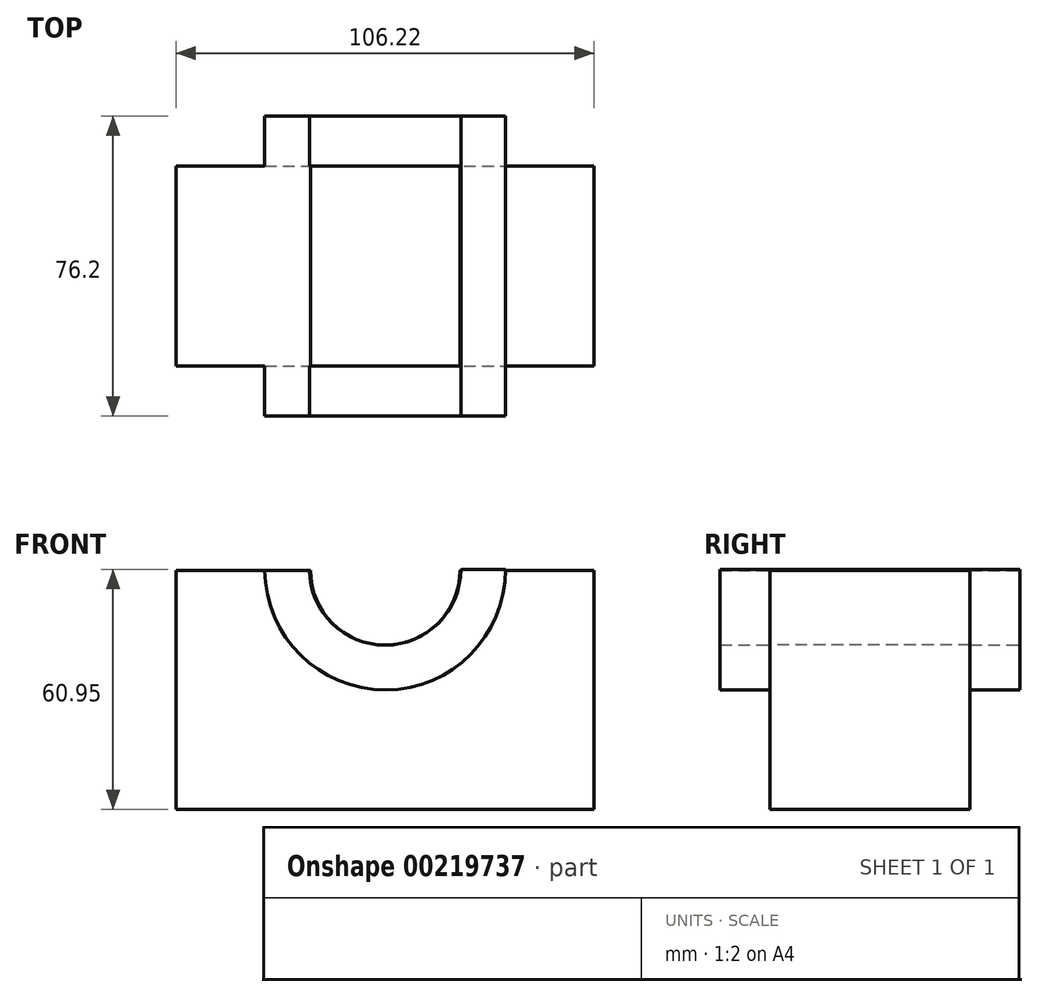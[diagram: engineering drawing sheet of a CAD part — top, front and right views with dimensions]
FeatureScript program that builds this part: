
annotation { "Feature Type Name" : "Feature", "Feature Type Description" : "" }
export const myFeature = defineFeature(function(context is Context, id is Id, definition is map)
    precondition{}
    {
        {
            var Q0;
            Q0=qCreatedBy(makeId("Front.planeOp"),FACE);
            var sketch = newSketch(context, id + "F0", { "sketchPlane" : qUnion([Q0])});
            skLineSegment(sketch, "E0.bottom", {"start": v(53.1, -30.36) * mm, "end": v(-53.1, -30.36) * mm});
            skLineSegment(sketch, "E0.left", {"start": v(53.1, -30.36) * mm, "end": v(53.1, 30.36) * mm});
            skLineSegment(sketch, "E0.right", {"start": v(-53.1, -30.36) * mm, "end": v(-53.1, 30.36) * mm});
            skPoint(sketch, "E0.middle", {"position": v(0, 0) * mm});
            skLineSegment(sketch, "E1", {"start": v(-53.1, 30.36) * mm, "end": v(53.1, 30.36) * mm});
            skSolve(sketch);
        }
        {
            var Q0;
            Q0=makeQuery(id+"F0.imprint","IMPRINT",FACE,{"disambiguationData":[TD([[makeQuery(id+"F0.imprint","IMPRINT",EDGE,{"derivedFrom":sQuery(id+"F0.wireOp",EDGE,"E0.bottom")}),-1.0]])]});
            extrude(context, id + "F1", {"entities" : qUnion([Q0]), "endBound" : BoundingType.SYMMETRIC, "depth" : 50.8 * mm});
        }
        {
            var Q0;
            Q0=qCreatedBy(makeId("Front.planeOp"),FACE);
            var sketch = newSketch(context, id + "F2", { "sketchPlane" : qUnion([Q0])});
            skArc(sketch, "E2", {"start": v(-30.6, 30.37) * mm, "mid": v(0.11, 0) * mm, "end": v(30.6, 30.6) * mm});
            skArc(sketch, "E3", {"start": v(-19.21, 30.37) * mm, "mid": v(0.11, 11.38) * mm, "end": v(19.21, 30.6) * mm});
            skLineSegment(sketch, "E4", {"start": v(-19.21, 30.37) * mm, "end": v(-30.6, 30.37) * mm});
            skLineSegment(sketch, "E5", {"start": v(19.21, 30.6) * mm, "end": v(30.6, 30.6) * mm});
            skSolve(sketch);
        }
        {
            var Q0;
            Q0 = qSketchRegion(id + "F2", true);
            extrude(context, id + "F3", {"entities" : qUnion([Q0]), "operationType" : NewBodyOperationType.ADD, "endBound" : BoundingType.SYMMETRIC, "depth" : 76.2 * mm});
        }
        {
            var Q0;
            {var subQ0=sQuery(id+"F0.wireOp",EDGE,"E1");Q0=makeQuery(id+"F3.boolean.opBoolean","SPLIT",FACE,{"disambiguationData":[TD([makeQuery(id+"F3.opExtrude","SWEPT_FACE",FACE,{"disambiguationData":[OSD([sQuery(id+"F2.wireOp",EDGE,"E3")])]})])],"derivedFrom":makeQuery(id+"F1.opExtrude","CAP_FACE",FACE,{"disambiguationData":[OSD([sQuery(id+"F0.wireOp",EDGE,"E0.bottom"),sQuery(id+"F0.wireOp",EDGE,"E0.left"),sQuery(id+"F0.wireOp",EDGE,"E0.right"),subQ0])],"isStart":false})});}
            var sketch = newSketch(context, id + "F4", { "sketchPlane" : qUnion([Q0])});
            skCircle(sketch, "E6", {"center": v(0, 30.36) * mm, "radius": 18.98 * mm});
            skSolve(sketch);
        }
        {
            var Q0;
            {var subQ0=sQuery(id+"F4.wireOp",EDGE,"E6");var subQ1=sQuery(id+"F0.wireOp",EDGE,"E1");var subQ2=makeQuery(id+"F1.opExtrude","CAP_FACE",FACE,{"disambiguationData":[OSD([sQuery(id+"F0.wireOp",EDGE,"E0.bottom"),sQuery(id+"F0.wireOp",EDGE,"E0.left"),sQuery(id+"F0.wireOp",EDGE,"E0.right"),subQ1])],"isStart":false});var subQ3=makeQuery(id+"F3.opExtrude","SWEPT_FACE",FACE,{"disambiguationData":[OSD([sQuery(id+"F2.wireOp",EDGE,"E3")])]});var subQ6=makeQuery(id+"F4.imprint","INTERSECT",VERTEX,{"derivedFrom":[makeQuery(id+"F3.boolean.opBoolean","INTERSECT",EDGE,{"derivedFrom":[subQ2,subQ3]}),subQ0]});Q0=makeQuery(id+"F4.imprint","IMPRINT",FACE,{"disambiguationData":[TD([[makeQuery(id+"F4.imprint","IMPRINT",EDGE,{"disambiguationData":[TD([[subQ6,1.0]])],"derivedFrom":subQ0}),1.0]])]});}
            var Q1;
            {var subQ0=sQuery(id+"F4.wireOp",EDGE,"E6");var subQ1=sQuery(id+"F0.wireOp",EDGE,"E1");var subQ2=makeQuery(id+"F3.boolean.opBoolean","SPLIT",EDGE,{"disambiguationData":[TD([makeQuery(id+"F3.opExtrude","SWEPT_FACE",FACE,{"disambiguationData":[OSD([sQuery(id+"F2.wireOp",EDGE,"E3")])]})])],"derivedFrom":makeQuery(id+"F1.opExtrude","CAP_EDGE",EDGE,{"disambiguationData":[OSD([subQ1])],"isStart":false})});var subQ3=makeQuery(id+"F4.imprint","INTERSECT",VERTEX,{"disambiguationData":[OD(0.0)],"derivedFrom":[subQ2,subQ0]});Q1=makeQuery(id+"F4.imprint","IMPRINT",FACE,{"disambiguationData":[TD([[makeQuery(id+"F4.imprint","IMPRINT",EDGE,{"disambiguationData":[TD([[subQ3,1.0]])],"derivedFrom":subQ0}),1.0]])]});}
            extrude(context, id + "F5", {"entities" : qUnion([Q0, Q1]), "operationType" : NewBodyOperationType.REMOVE, "oppositeDirection" : true, "depth" : 152.4 * mm});
        }
    });
